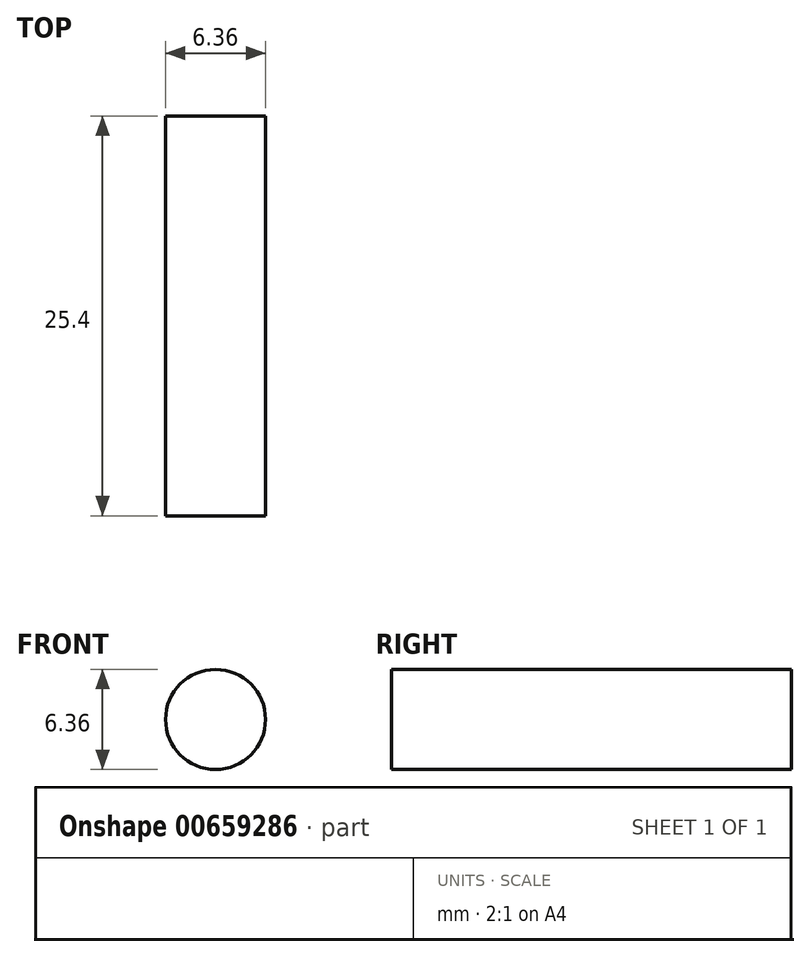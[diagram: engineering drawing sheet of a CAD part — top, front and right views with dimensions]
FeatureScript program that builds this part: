
annotation { "Feature Type Name" : "Feature", "Feature Type Description" : "" }
export const myFeature = defineFeature(function(context is Context, id is Id, definition is map)
    precondition{}
    {
        {
            var Q0;
            Q0=qCreatedBy(makeId("Front.planeOp"),FACE);
            var sketch = newSketch(context, id + "F0", { "sketchPlane" : qUnion([Q0])});
            skCircle(sketch, "E0", {"center": v(0, 0) * mm, "radius": 3.18 * mm});
            skSolve(sketch);
        }
        {
            var Q0;
            Q0 = qSketchRegion(id + "F0", true);
            extrude(context, id + "F1", {"entities" : qUnion([Q0]), "depth" : 25.4 * mm, "offsetDistance" : 25.4 * mm});
        }
    });
